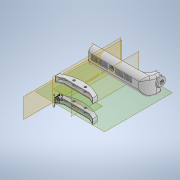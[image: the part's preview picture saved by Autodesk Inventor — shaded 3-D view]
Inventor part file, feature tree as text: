
AUTODESK INVENTOR PART (.ipt)
format: ipt  version: 2021 (Build 250183000, 183)  size: 591,360 bytes
history: native  units: mm
features: sketch x6, plane x6, mirror x5, extrude x3, sweep x1, projected_geometry x1, other x1
ambient origin geometry x8: Origin, YZ Plane, XZ Plane, XY Plane, X Axis, Y Axis, Z Axis, Center Point
bodies: Solid1 (feature_tree)
feature tree (23):
  sketch  "Sketch7"  dims[d10=10.0mm d11=31.4mm]
  plane  "Work Plane4"
  sketch  "Sketch8"  dims[d13=100.0mm d33=100.0mm]
  plane  "Work Plane5"
  plane  "Work Plane7"
  mirror  "Mirror4"
  sweep  "Sweep5"
  sketch  "Sketch15"  dims[d38=7.0mm d39=1.0mm]
  plane  "Work Plane13"
  extrude  "Extrusion7"  Depth=100.0mm
  mirror  "Mirror6"
  mirror  "Mirror7"
  extrude  "Extrusion8"  Depth=100.0mm
  plane  "Work Plane14"
  mirror  "Mirror8"
  mirror  "Mirror9"
  extrude  "Extrusion9"  Depth=1.0mm
  plane  "Work Plane9"
  sketch  "Sketch13"  dims[d36=100.0mm d37=100.0mm]
  projected_geometry  "Projected Loop5"
  sketch  "Sketch16"  dims[d40=9.0mm]
  sketch  "Sketch17"  dims[d41=1.0mm d42=9.0mm d43=3.5mm d44=1.0mm d45=3.5mm d46=1.0mm d47=1.0mm d48=5.0mm d49=1.0mm d50=5.0mm d71=0.0mm d72=0.0mm d75=1.0mm d76=0.0mm d77=1.0mm d78=0.0mm d79=3.0mm d80=3.0mm d81=38.5mm d82=0.0mm]
  other  "Cavity6"
